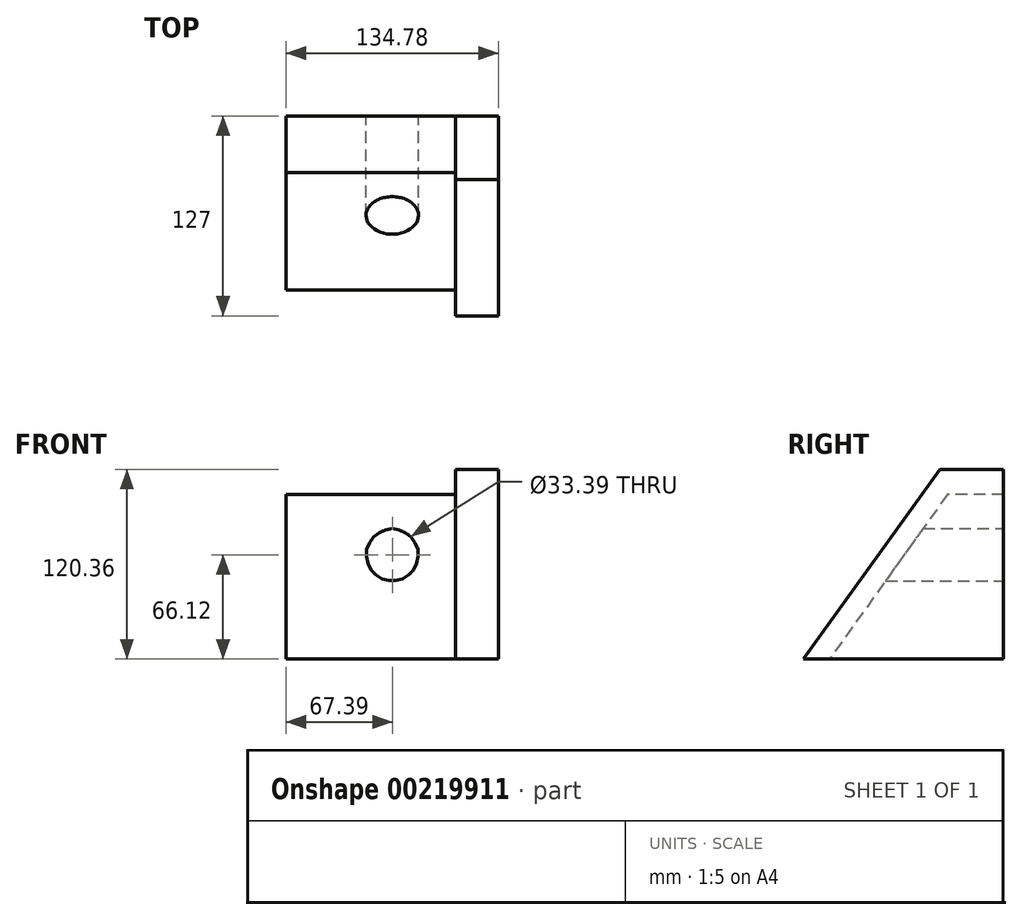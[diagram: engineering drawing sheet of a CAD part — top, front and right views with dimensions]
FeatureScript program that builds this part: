
annotation { "Feature Type Name" : "Feature", "Feature Type Description" : "" }
export const myFeature = defineFeature(function(context is Context, id is Id, definition is map)
    precondition{}
    {
        {
            var Q0;
            Q0=qCreatedBy(makeId("Front.planeOp"),FACE);
            var sketch = newSketch(context, id + "F0", { "sketchPlane" : qUnion([Q0])});
            skCircle(sketch, "E0", {"center": v(0, 0) * mm, "radius": 16.7 * mm});
            skLineSegment(sketch, "E1", {"start": v(0, 54.24) * mm, "end": v(-67.4, 54.24) * mm});
            skLineSegment(sketch, "E2", {"start": v(-67.4, -66.12) * mm, "end": v(0, -66.12) * mm});
            skLineSegment(sketch, "E3", {"start": v(-67.4, 54.24) * mm, "end": v(-67.4, -66.12) * mm});
            skLineSegment(sketch, "E4.MirrorCS", {"start": v(0, 54.24) * mm, "end": v(67.4, 54.24) * mm});
            skLineSegment(sketch, "E5.MirrorCS", {"start": v(67.4, -66.12) * mm, "end": v(0, -66.12) * mm});
            skLineSegment(sketch, "E6.MirrorCS", {"start": v(67.4, 54.24) * mm, "end": v(67.4, -66.12) * mm});
            skSolve(sketch);
        }
        {
            var Q0;
            Q0=makeQuery(id+"F0.imprint","IMPRINT",FACE,{"disambiguationData":[TD([[makeQuery(id+"F0.imprint","IMPRINT",EDGE,{"derivedFrom":sQuery(id+"F0.wireOp",EDGE,"E0")}),-1.0]])]});
            extrude(context, id + "F1", {"entities" : qUnion([Q0]), "depth" : 127 * mm});
        }
        {
            var Q0;
            Q0=makeQuery(id+"F1.opExtrude","SWEPT_FACE",FACE,{"disambiguationData":[OSD([sQuery(id+"F0.wireOp",EDGE,"E3")])]});
            var sketch = newSketch(context, id + "F2", { "sketchPlane" : qUnion([Q0])});
            skLineSegment(sketch, "E7", {"start": v(0, 54.24) * mm, "end": v(40.4, 54.24) * mm});
            skLineSegment(sketch, "E8", {"start": v(40.4, 54.24) * mm, "end": v(127, -66.12) * mm});
            skLineSegment(sketch, "E9", {"start": v(127, -66.12) * mm, "end": v(0, -66.12) * mm});
            skLineSegment(sketch, "E10", {"start": v(0, -66.12) * mm, "end": v(0, 54.24) * mm});
            skSolve(sketch);
        }
        {
            var Q0;
            {var subQ0=sQuery(id+"F2.wireOp",EDGE,"E8");Q0=makeQuery(id+"F2.imprint","IMPRINT",FACE,{"disambiguationData":[TD([[makeQuery(id+"F2.imprint","IMPRINT",EDGE,{"derivedFrom":subQ0}),1.0]])]});}
            extrude(context, id + "F3", {"entities" : qUnion([Q0]), "operationType" : NewBodyOperationType.REMOVE, "oppositeDirection" : true, "depth" : 136.14 * mm});
        }
        {
            var Q0;
            Q0=makeQuery(id+"F1.opExtrude","SWEPT_FACE",FACE,{"disambiguationData":[OSD([sQuery(id+"F0.wireOp",EDGE,"E3")])]});
            var sketch = newSketch(context, id + "F4", { "sketchPlane" : qUnion([Q0])});
            skLineSegment(sketch, "E11", {"start": v(0, 38.3) * mm, "end": v(35.8, 38.3) * mm});
            skLineSegment(sketch, "E12", {"start": v(35.8, 38.3) * mm, "end": v(110.43, -66.12) * mm});
            skLineSegment(sketch, "E13", {"start": v(110.43, -66.12) * mm, "end": v(0, -66.12) * mm});
            skLineSegment(sketch, "E14", {"start": v(0, -66.12) * mm, "end": v(0, 38.3) * mm});
            skSolve(sketch);
        }
        {
            var Q0;
            {var subQ3=sQuery(id+"F4.wireOp",EDGE,"E11");Q0=makeQuery(id+"F4.imprint","IMPRINT",FACE,{"disambiguationData":[TD([[makeQuery(id+"F4.imprint","IMPRINT",EDGE,{"derivedFrom":subQ3}),1.0]])]});}
            extrude(context, id + "F5", {"entities" : qUnion([Q0]), "operationType" : NewBodyOperationType.REMOVE, "oppositeDirection" : true, "depth" : 107.7 * mm});
        }
    });
